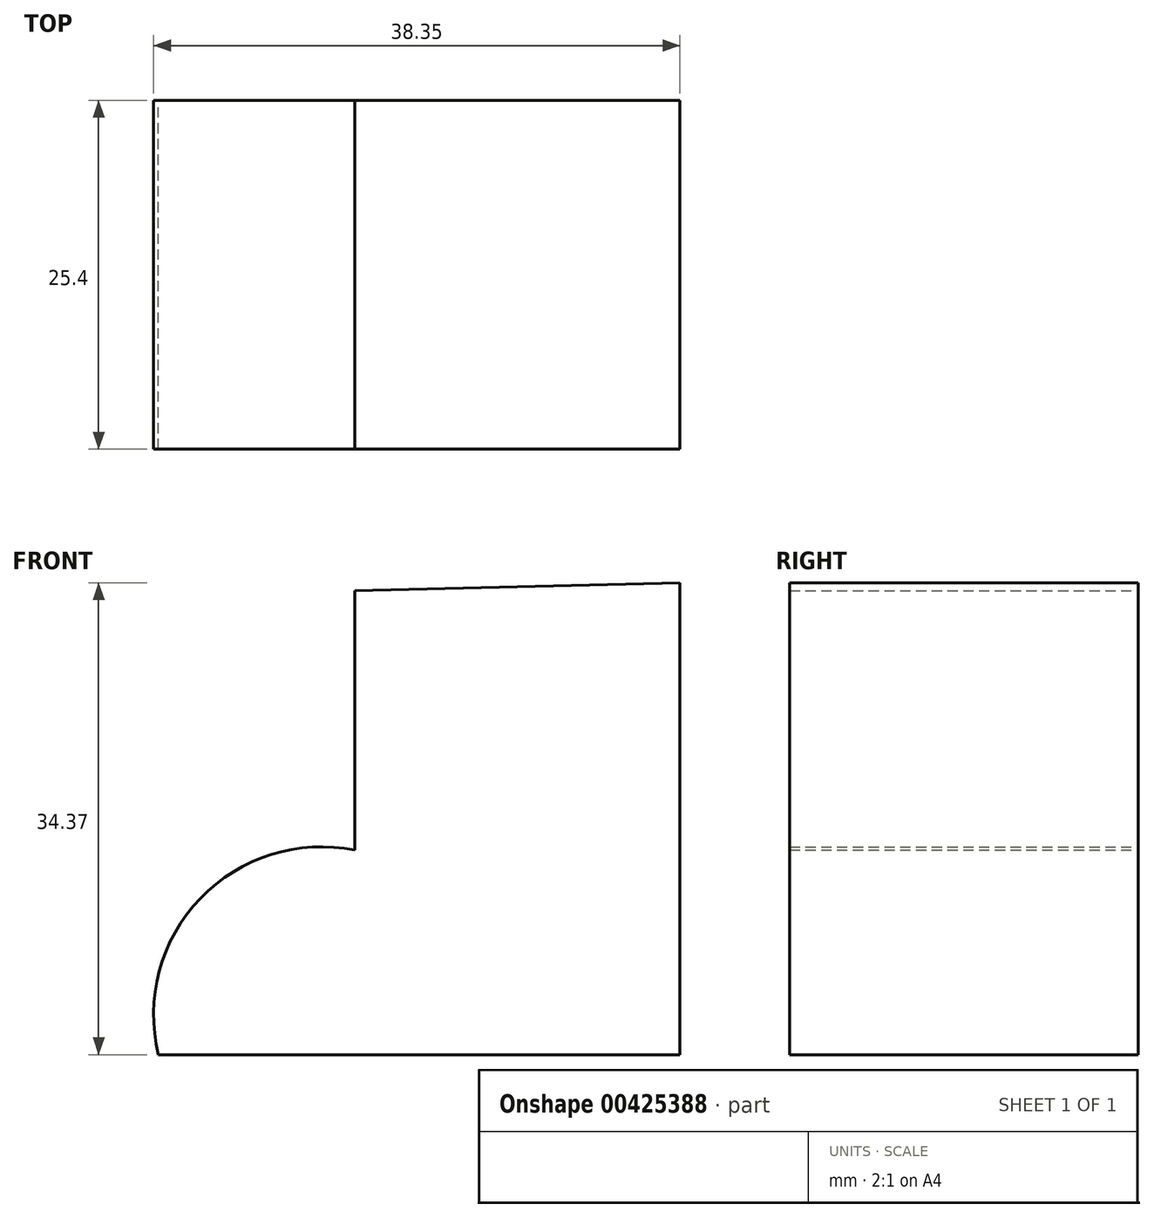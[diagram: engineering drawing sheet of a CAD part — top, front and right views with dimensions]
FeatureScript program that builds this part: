
annotation { "Feature Type Name" : "Feature", "Feature Type Description" : "" }
export const myFeature = defineFeature(function(context is Context, id is Id, definition is map)
    precondition{}
    {
        {
            var Q0;
            Q0=qCreatedBy(makeId("Front.planeOp"),FACE);
            var sketch = newSketch(context, id + "F0", { "sketchPlane" : qUnion([Q0])});
            skLineSegment(sketch, "E0", {"start": v(0, 34.37) * mm, "end": v(0, 0) * mm});
            skLineSegment(sketch, "E1", {"start": v(0, 0) * mm, "end": v(-38, 0) * mm});
            skArc(sketch, "E2", {"start": v(-23.68, 14.9) * mm, "mid": v(-34.94, 11.4) * mm, "end": v(-38, 0) * mm});
            skLineSegment(sketch, "E3", {"start": v(-23.68, 14.9) * mm, "end": v(-23.68, 33.8) * mm});
            skLineSegment(sketch, "E4", {"start": v(-23.68, 33.8) * mm, "end": v(0, 34.37) * mm});
            skSolve(sketch);
        }
        {
            var Q0;
            Q0=makeQuery(id+"F0.imprint","IMPRINT",FACE,{"disambiguationData":[TD([[makeQuery(id+"F0.imprint","IMPRINT",EDGE,{"derivedFrom":sQuery(id+"F0.wireOp",EDGE,"E0")}),-1.0]])]});
            extrude(context, id + "F1", {"entities" : qUnion([Q0]), "depth" : 25.4 * mm});
        }
    });
